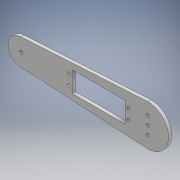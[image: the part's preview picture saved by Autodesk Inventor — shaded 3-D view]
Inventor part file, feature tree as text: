
AUTODESK INVENTOR PART (.ipt)
format: ipt  version: 2018 (Build 220112000, 112)  size: 124,928 bytes
history: native  units: mm
features: other x1, extrude x1, sketch x1
ambient origin geometry x8: Origin, YZ Plane, XZ Plane, XY Plane, X Axis, Y Axis, Z Axis, Center Point
bodies: Body1 (feature_tree)
feature tree (3):
  other  "Sólido1"
  extrude  "Extrusión1"  Depth=3.0mm
  sketch  "Boceto1"  dims[d15=39.0mm d26=30.0mm d102=5.0mm d107=3.0mm d108=3.0mm d110=3.0mm d112=3.0mm d113=3.0mm d114=0.0mm]
